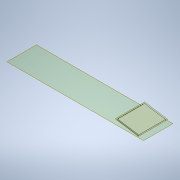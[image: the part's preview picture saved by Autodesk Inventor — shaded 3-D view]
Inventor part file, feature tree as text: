
AUTODESK INVENTOR PART (.ipt)
format: ipt  version: 2020.2 (Build 242310000, 310)  size: 121,344 bytes
history: native  units: mm
features: extrude x3, sketch x3, other x2
ambient origin geometry x8: Origin, YZ Plane, XZ Plane, XY Plane, X Axis, Y Axis, Z Axis, Center Point
bodies: Solide1 (feature_tree)
feature tree (8):
  extrude  "Extrusion1"  Depth=785.7mm
  other  "Plan de construction1"
  extrude  "Extrusion2"  Depth=3.0mm
  other  "Plan de construction2"
  extrude  "Extrusion3"  Depth=65.0mm TaperAngle=0.0deg
  sketch  "Esquisse1"
  sketch  "Esquisse2"
  sketch  "Esquisse3"
